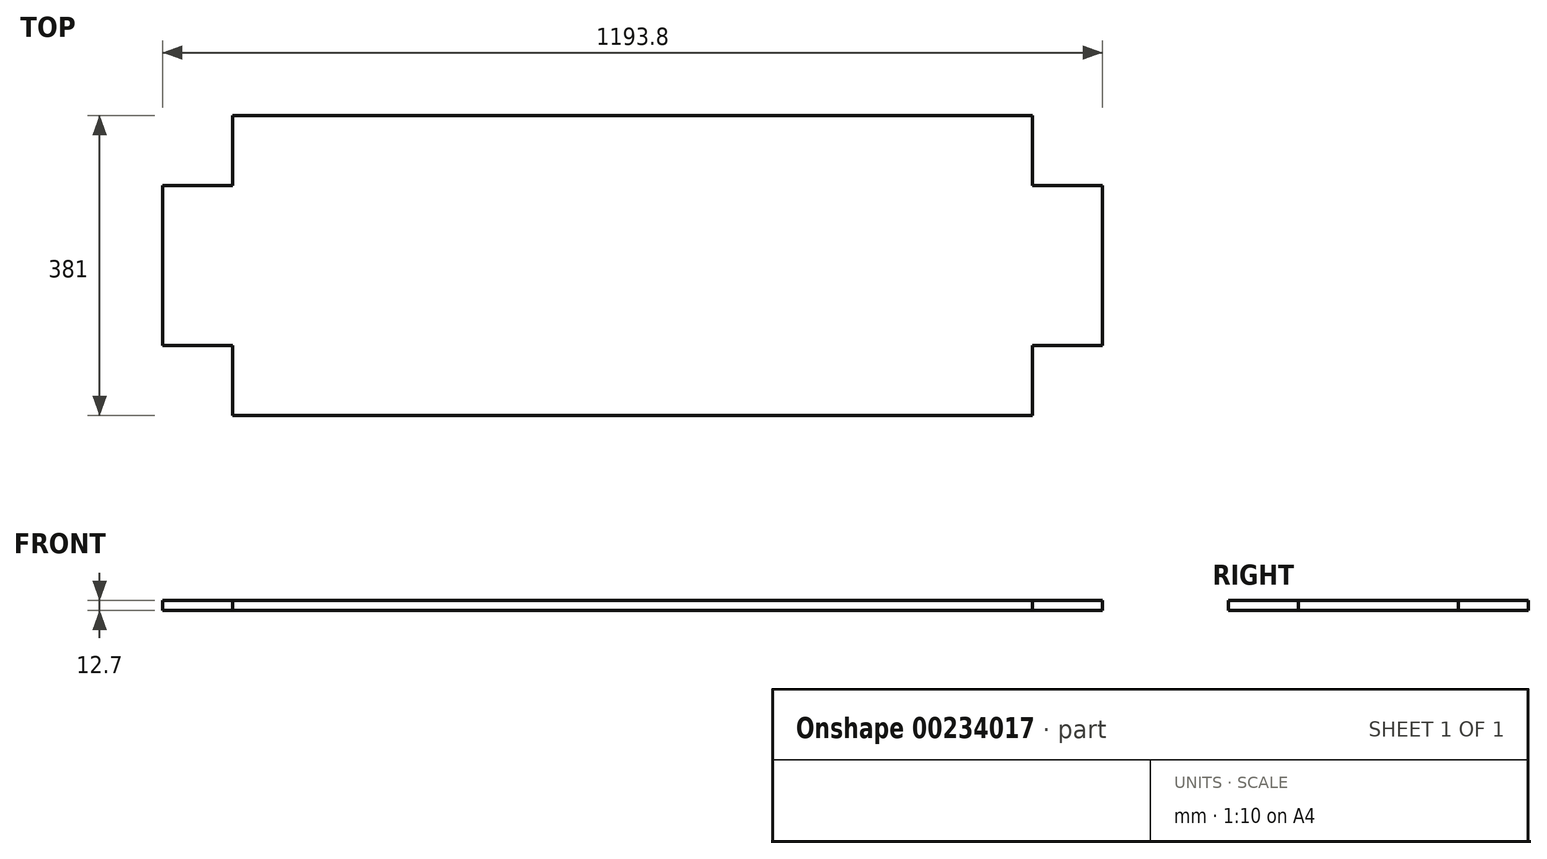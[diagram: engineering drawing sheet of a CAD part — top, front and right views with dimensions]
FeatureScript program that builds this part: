
annotation { "Feature Type Name" : "Feature", "Feature Type Description" : "" }
export const myFeature = defineFeature(function(context is Context, id is Id, definition is map)
    precondition{}
    {
        {
            var Q0;
            Q0=qCreatedBy(makeId("Top.planeOp"),FACE);
            var sketch = newSketch(context, id + "F0", { "sketchPlane" : qUnion([Q0])});
            skLineSegment(sketch, "E0.bottom", {"start": v(-508, 190.5) * mm, "end": v(508, 190.5) * mm});
            skLineSegment(sketch, "E0.top", {"start": v(-508, -190.5) * mm, "end": v(508, -190.5) * mm});
            skLineSegment(sketch, "E0.left", {"start": v(-596.9, 101.6) * mm, "end": v(-596.9, -101.6) * mm});
            skLineSegment(sketch, "E0.right", {"start": v(596.9, 101.6) * mm, "end": v(596.9, -101.6) * mm});
            skPoint(sketch, "E0.middle", {"position": v(0, 0) * mm});
            skLineSegment(sketch, "E1.top", {"start": v(596.9, 101.6) * mm, "end": v(508, 101.6) * mm});
            skLineSegment(sketch, "E1.right", {"start": v(508, 190.5) * mm, "end": v(508, 101.6) * mm});
            skLineSegment(sketch, "E2.top", {"start": v(596.9, -101.6) * mm, "end": v(508, -101.6) * mm});
            skLineSegment(sketch, "E2.right", {"start": v(508, -190.5) * mm, "end": v(508, -101.6) * mm});
            skLineSegment(sketch, "E3.top", {"start": v(-596.9, -101.6) * mm, "end": v(-508, -101.6) * mm});
            skLineSegment(sketch, "E3.right", {"start": v(-508, -190.5) * mm, "end": v(-508, -101.6) * mm});
            skLineSegment(sketch, "E4.top", {"start": v(-596.9, 101.6) * mm, "end": v(-508, 101.6) * mm});
            skLineSegment(sketch, "E4.right", {"start": v(-508, 190.5) * mm, "end": v(-508, 101.6) * mm});
            skPoint(sketch, "E5.orphan", {"position": v(596.9, 190.5) * mm});
            skPoint(sketch, "E6.orphan", {"position": v(596.9, -190.5) * mm});
            skPoint(sketch, "E7.orphan", {"position": v(-596.9, -190.5) * mm});
            skPoint(sketch, "E8.orphan", {"position": v(-596.9, 190.5) * mm});
            skSolve(sketch);
        }
        {
            var Q0;
            Q0 = qSketchRegion(id + "F0", true);
            extrude(context, id + "F1", {"entities" : qUnion([Q0]), "depth" : 12.7 * mm});
        }
    });
